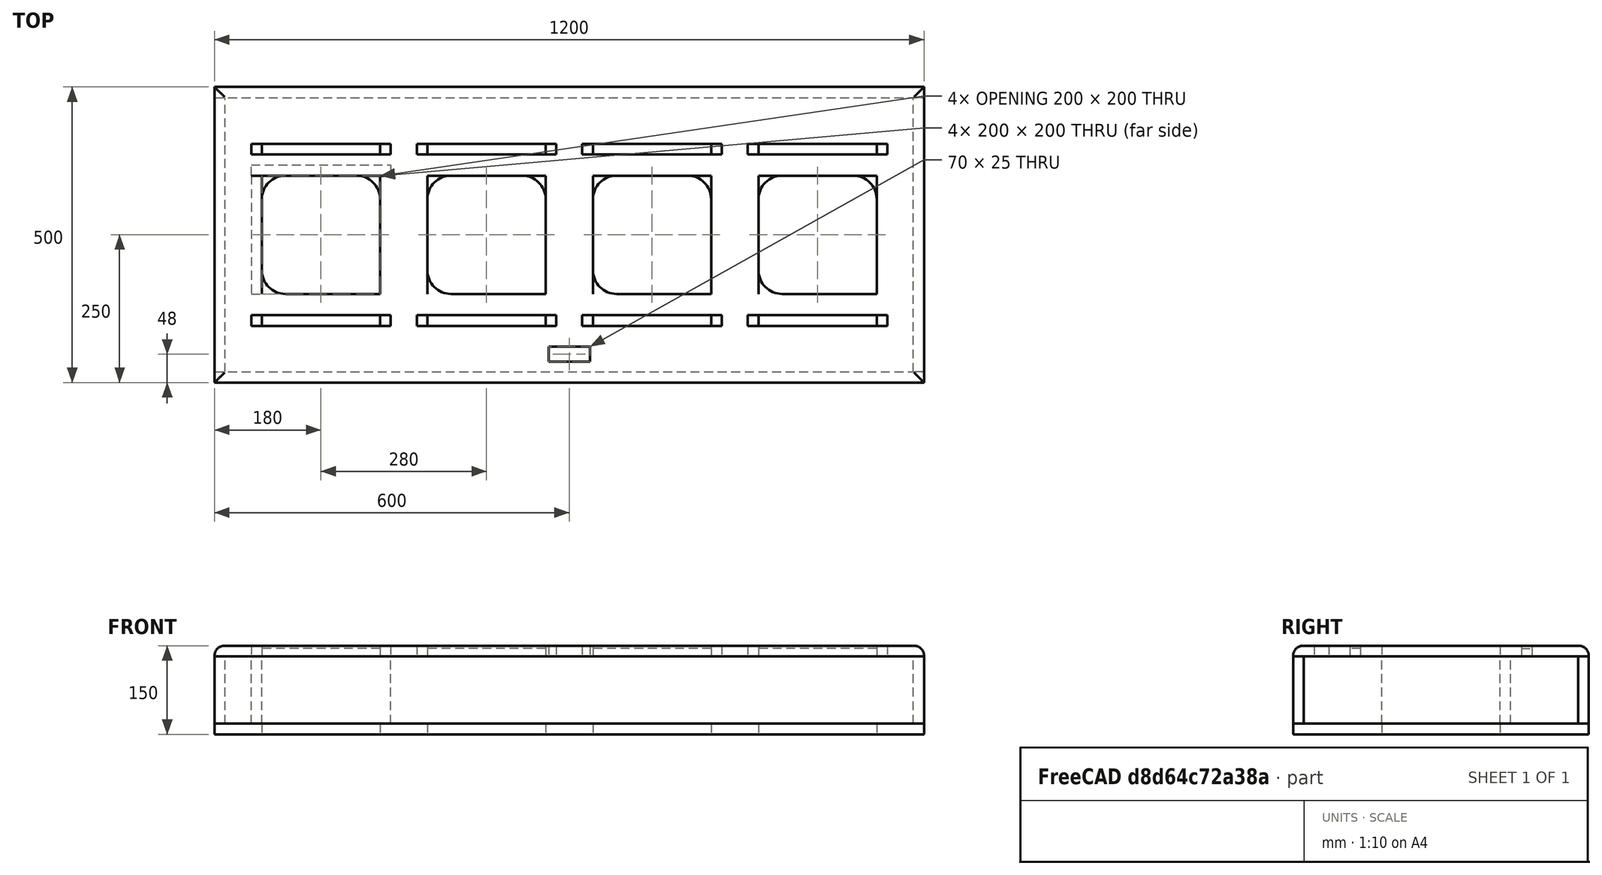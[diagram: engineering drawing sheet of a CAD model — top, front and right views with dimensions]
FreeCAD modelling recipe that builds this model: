
FCSTD DOCUMENT  (FreeCAD 0.18R16093 (Git))
Label: TonneV2
License: All rights reserved
LicenseURL: http://en.wikipedia.org/wiki/All_rights_reserved
objects: Sketcher::SketchObject×11, PartDesign::Body×8, TechDraw::DrawViewDimension×8, PartDesign::Pad×7, PartDesign::Pocket×4, PartDesign::LinearPattern×4, PartDesign::Mirrored×3, PartDesign::ShapeBinder×2, PartDesign::MultiTransform×2, PartDesign::Fillet×2, Spreadsheet::Sheet×1, PartDesign::FeatureBase×1, TechDraw::DrawSVGTemplate×1, TechDraw::DrawViewPart×1, TechDraw::DrawPage×1, App::DocumentObjectGroup×1
note: 55 computed .brp shape members not serialized (recipe doc carries the construction recipe); baked Part::Feature solids carry a one-line shape summary decoded from their .brp

FEATURE [Spreadsheet::Sheet] Spreadsheet  label="S"
  cells = A1=Höhe:; B1(Hoehe)=150; A2=Breite:; B2(Breite)=1200; A3=Tiefe:; B3(Tiefe)=500; A4=Materialdicke:; B4(Materialdicke)=18; A5=RandabstandLoch; B5(RandabstandLoch)=80; A6=Loch; B6(Loch)=200
FEATURE [Sketcher::SketchObject] Sketch
  MapMode = 5
  Support = -> [XY_Plane005]
  sketch-geometry (4):
    g0: LineSegment StartX=-600 StartY=250 StartZ=0 EndX=600 EndY=250 EndZ=0
    g1: LineSegment StartX=600 StartY=250 StartZ=0 EndX=600 EndY=-250 EndZ=0
    g2: LineSegment StartX=600 StartY=-250 StartZ=0 EndX=-600 EndY=-250 EndZ=0
    g3: LineSegment StartX=-600 StartY=-250 StartZ=0 EndX=-600 EndY=250 EndZ=0
  constraints (11):
    c: Coincident(g0,g1)
    c: Coincident(g1,g2)
    c: Coincident(g2,g3)
    c: Coincident(g3,g0)
    c: Horizontal(g0)
    c: Horizontal(g2)
    c: Vertical(g1)
    c: Vertical(g3)
    c: Symmetric(g1,g0,g-1)
    c: Distance(g0) = 1200
    c: Distance(g1) = 500
FEATURE [PartDesign::Pad] Pad
  Length = 18
  Length2 = 100
  Profile = -> Sketch
  Type = 0
FEATURE [Sketcher::SketchObject] Sketch006
  ExternalGeometry = -> [Pad]
  MapMode = 5
  Placement = pos=(0,0,18) rot=(0,0,1;0rad)
  Support = -> [Pad]
  sketch-geometry (4):
    g0: LineSegment StartX=-520 StartY=100 StartZ=0 EndX=-320 EndY=100 EndZ=0
    g1: LineSegment StartX=-320 StartY=100 StartZ=0 EndX=-320 EndY=-100 EndZ=0
    g2: LineSegment StartX=-320 StartY=-100 StartZ=0 EndX=-520 EndY=-100 EndZ=0
    g3: LineSegment StartX=-520 StartY=-100 StartZ=0 EndX=-520 EndY=100 EndZ=0
  constraints (12):
    c: Coincident(g0,g1)
    c: Coincident(g1,g2)
    c: Coincident(g2,g3)
    c: Coincident(g3,g0)
    c: Horizontal(g0)
    c: Horizontal(g2)
    c: Vertical(g1)
    c: Vertical(g3)
    c: Equal(g1,g2)
    c: Symmetric(g0,g1,g-1)
    c: Distance(g0) = 200
    c: DistanceX(g-3,g0) = 80
FEATURE [PartDesign::Pocket] Pocket
  BaseFeature = -> Pad
  Length = 5
  Length2 = 100
  Profile = -> Sketch006
  Type = 2
FEATURE [PartDesign::LinearPattern] LinearPattern
  BaseFeature = -> Pocket
  Direction = -> Sketch006 [H_Axis]
  Length = 840
  Occurrences = 4
  Originals = -> [Pocket]
FEATURE [PartDesign::Body] Body005  label="Boden"
  Group = -> [Sketch,Pad,Sketch006,Pocket,LinearPattern]
  Origin = -> Origin005
  Tip = -> LinearPattern
FEATURE [PartDesign::FeatureBase] BaseFeature
  BaseFeature = -> LinearPattern
FEATURE [Sketcher::SketchObject] Sketch007
  MapMode = 5
  Placement = pos=(0,0,0) rot=(1,0,0;1.5708rad)
  Support = -> [XZ_Plane006]
  sketch-geometry (4):
    g0: LineSegment StartX=-600 StartY=0 StartZ=0 EndX=600 EndY=0 EndZ=0
    g1: LineSegment StartX=600 StartY=0 StartZ=0 EndX=600 EndY=114 EndZ=0
    g2: LineSegment StartX=600 StartY=114 StartZ=0 EndX=-600 EndY=114 EndZ=0
    g3: LineSegment StartX=-600 StartY=114 StartZ=0 EndX=-600 EndY=0 EndZ=0
  constraints (11):
    c: Coincident(g0,g1)
    c: Coincident(g1,g2)
    c: Coincident(g2,g3)
    c: Coincident(g3,g0)
    c: Horizontal(g0)
    c: Horizontal(g2)
    c: Vertical(g1)
    c: Vertical(g3)
    c: Distance(g0) = 1200
    c: Distance(g3) = 114
    c: Symmetric(g0,g0,g-1)
FEATURE [PartDesign::Pad] Pad001
  Length = 18
  Length2 = 100
  Placement = pos=(0,0,0) rot=(1,0,0;1.5708rad)
  Profile = -> Sketch007
  Type = 0
FEATURE [PartDesign::Body] Body006  label="Backplate"
  Group = -> [Sketch007,Pad001]
  Origin = -> Origin006
  Placement = pos=(0,250,18) rot=(0,0,1;0rad)
  Tip = -> Pad001
FEATURE [Sketcher::SketchObject] Sketch008
  MapMode = 2
  Placement = pos=(0,0,0) rot=(1,0,0;1.5708rad)
  Support = -> [XZ_Plane007]
  sketch-geometry (4):
    g0: LineSegment StartX=-600 StartY=18 StartZ=0 EndX=600 EndY=18 EndZ=0
    g1: LineSegment StartX=600 StartY=18 StartZ=0 EndX=600 EndY=132 EndZ=0
    g2: LineSegment StartX=600 StartY=132 StartZ=0 EndX=-600 EndY=132 EndZ=0
    g3: LineSegment StartX=-600 StartY=132 StartZ=0 EndX=-600 EndY=18 EndZ=0
  constraints (12):
    c: Coincident(g0,g1)
    c: Coincident(g1,g2)
    c: Coincident(g2,g3)
    c: Coincident(g3,g0)
    c: Horizontal(g0)
    c: Horizontal(g2)
    c: Vertical(g1)
    c: Vertical(g3)
    c: Distance(g0) = 1200
    c: DistanceY(g-1,g0) = 18
    c: Distance(g3) = 114
    c: Symmetric(g0,g0,g-2)
FEATURE [PartDesign::Pad] Pad002
  Length = 18
  Length2 = 100
  Placement = pos=(0,0,0) rot=(1,0,0;1.5708rad)
  Profile = -> Sketch008
  Type = 0
FEATURE [PartDesign::Body] Body007  label="Faceplate"
  Group = -> [Sketch008,Pad002]
  Origin = -> Origin007
  Placement = pos=(0,-232,0) rot=(1,0,0;0rad)
  Tip = -> Pad002
FEATURE [Sketcher::SketchObject] Sketch009
  MapMode = 5
  Placement = pos=(0,0,0) rot=(0.57735,0.57735,0.57735;2.0944rad)
  Support = -> [YZ_Plane008]
  sketch-geometry (4):
    g0: LineSegment StartX=-232 StartY=0 StartZ=0 EndX=232 EndY=0 EndZ=0
    g1: LineSegment StartX=232 StartY=0 StartZ=0 EndX=232 EndY=114 EndZ=0
    g2: LineSegment StartX=232 StartY=114 StartZ=0 EndX=-232 EndY=114 EndZ=0
    g3: LineSegment StartX=-232 StartY=114 StartZ=0 EndX=-232 EndY=0 EndZ=0
  constraints (11):
    c: Coincident(g0,g1)
    c: Coincident(g1,g2)
    c: Coincident(g2,g3)
    c: Coincident(g3,g0)
    c: Horizontal(g0)
    c: Horizontal(g2)
    c: Vertical(g1)
    c: Vertical(g3)
    c: Distance(g0) = 464
    c: Distance(g1) = 114
    c: Symmetric(g0,g0,g-1)
FEATURE [PartDesign::Pad] Pad003
  Length = 18
  Length2 = 100
  Placement = pos=(0,0,0) rot=(0.57735,0.57735,0.57735;2.0944rad)
  Profile = -> Sketch009
  Reversed = true
  Type = 0
FEATURE [PartDesign::Body] Body008  label="Rechts"
  Group = -> [Sketch009,Pad003]
  Origin = -> Origin008
  Placement = pos=(600,0,18) rot=(0,0,1;0rad)
  Tip = -> Pad003
FEATURE [Sketcher::SketchObject] Sketch011
  MapMode = 5
  Placement = pos=(0,0,0) rot=(0.57735,0.57735,0.57735;2.0944rad)
  Support = -> [YZ_Plane009]
  sketch-geometry (4):
    g0: LineSegment StartX=-232 StartY=0 StartZ=0 EndX=232 EndY=0 EndZ=0
    g1: LineSegment StartX=232 StartY=0 StartZ=0 EndX=232 EndY=114 EndZ=0
    g2: LineSegment StartX=232 StartY=114 StartZ=0 EndX=-232 EndY=114 EndZ=0
    g3: LineSegment StartX=-232 StartY=114 StartZ=0 EndX=-232 EndY=0 EndZ=0
  constraints (11):
    c: Coincident(g0,g1)
    c: Coincident(g1,g2)
    c: Coincident(g2,g3)
    c: Coincident(g3,g0)
    c: Horizontal(g0)
    c: Horizontal(g2)
    c: Vertical(g1)
    c: Vertical(g3)
    c: Distance(g0) = 464
    c: Distance(g1) = 114
    c: Symmetric(g0,g0,g-1)
FEATURE [PartDesign::Pad] Pad004
  Length = 18
  Length2 = 100
  Placement = pos=(0,0,0) rot=(0.57735,0.57735,0.57735;2.0944rad)
  Profile = -> Sketch011
  Type = 0
FEATURE [PartDesign::Body] Body009  label="Links"
  Group = -> [Sketch011,Pad004]
  Origin = -> Origin009
  Placement = pos=(-600,0,18) rot=(0,0,1;0rad)
  Tip = -> Pad004
FEATURE [PartDesign::ShapeBinder] ShapeBinder
  Support = -> [LinearPattern]
  TraceSupport = false
FEATURE [Sketcher::SketchObject] Sketch012
  ExternalGeometry = -> [ShapeBinder]
  MapMode = 5
  Placement = pos=(0,0,18) rot=(0,0,1;0rad)
  Support = -> [ShapeBinder]
  sketch-geometry (4):
    g0: LineSegment StartX=-520 StartY=100 StartZ=0 EndX=-538 EndY=100 EndZ=0
    g1: LineSegment StartX=-538 StartY=100 StartZ=0 EndX=-538 EndY=-100 EndZ=0
    g2: LineSegment StartX=-538 StartY=-100 StartZ=0 EndX=-520 EndY=-100 EndZ=0
    g3: LineSegment StartX=-520 StartY=-100 StartZ=0 EndX=-520 EndY=100 EndZ=0
  constraints (11):
    c: Coincident(g0,g1)
    c: Coincident(g1,g2)
    c: Coincident(g3,g0)
    c: Horizontal(g0)
    c: Horizontal(g2)
    c: Vertical(g3)
    c: Coincident(g0,g-3)
    c: Distance(g0) = 18
    c: Coincident(g2,g3)
    c: Coincident(g-3,g2)
    c: Vertical(g1)
FEATURE [PartDesign::Pad] Pad005
  Length = 114
  Length2 = 100
  Profile = -> Sketch012
  Type = 0
FEATURE [PartDesign::Body] Body010  label="LochAbdeckungLinks"
  Group = -> [ShapeBinder,Sketch012,Pad005]
  Origin = -> Origin010
  Tip = -> Pad005
FEATURE [PartDesign::ShapeBinder] ShapeBinder001
  Support = -> [LinearPattern]
  TraceSupport = false
FEATURE [Sketcher::SketchObject] Sketch013
  ExternalGeometry = -> [ShapeBinder001]
  MapMode = 5
  Placement = pos=(0,0,18) rot=(0,0,1;0rad)
  Support = -> [ShapeBinder001]
  sketch-geometry (5):
    g0: LineSegment StartX=-538 StartY=118 StartZ=0 EndX=-302 EndY=118 EndZ=0
    g1: LineSegment StartX=-302 StartY=118 StartZ=0 EndX=-302 EndY=100 EndZ=0
    g2: LineSegment StartX=-302 StartY=100 StartZ=0 EndX=-538 EndY=100 EndZ=0
    g3: LineSegment StartX=-538 StartY=100 StartZ=0 EndX=-538 EndY=118 EndZ=0
    g4: LineSegment [constr] StartX=-420 StartY=125 StartZ=0 EndX=-420 EndY=75 EndZ=0
  constraints (15):
    c: Coincident(g0,g1)
    c: Coincident(g1,g2)
    c: Coincident(g2,g3)
    c: Coincident(g3,g0)
    c: Horizontal(g0)
    c: Horizontal(g2)
    c: Vertical(g1)
    c: Vertical(g3)
    c: PointOnObject(g-3,g2)
    c: Distance(g2,g-3) = 18
    c: Distance(g1) = 18
    c: Distance(g4) = 50
    c: Symmetric(g4,g4,g-3)
    c: Symmetric(g-3,g-3,g4)
    c: Symmetric(g1,g2,g4)
FEATURE [PartDesign::Pad] Pad006
  Length = 114
  Length2 = 100
  Profile = -> Sketch013
  Type = 0
FEATURE [PartDesign::Body] Body011  label="LochAbdeckungOben"
  Group = -> [ShapeBinder001,Sketch013,Pad006]
  Origin = -> Origin011
  Tip = -> Pad006
FEATURE [Sketcher::SketchObject] Sketch014
  ExternalGeometry = -> [BaseFeature]
  MapMode = 5
  Placement = pos=(0,0,18) rot=(0,0,1;0rad)
  Support = -> [BaseFeature]
  sketch-geometry (6):
    g0: LineSegment StartX=-538 StartY=154 StartZ=0 EndX=-302 EndY=154 EndZ=0
    g1: LineSegment StartX=-302 StartY=154 StartZ=0 EndX=-302 EndY=136 EndZ=0
    g2: LineSegment StartX=-302 StartY=136 StartZ=0 EndX=-538 EndY=136 EndZ=0
    g3: LineSegment StartX=-538 StartY=136 StartZ=0 EndX=-538 EndY=154 EndZ=0
    g4: LineSegment [constr] StartX=-538 StartY=136 StartZ=0 EndX=-520 EndY=100 EndZ=0
    g5: LineSegment [constr] StartX=-302 StartY=136 StartZ=0 EndX=-320 EndY=100 EndZ=0
  constraints (16):
    c: Coincident(g0,g1)
    c: Coincident(g1,g2)
    c: Coincident(g2,g3)
    c: Coincident(g3,g0)
    c: Horizontal(g0)
    c: Horizontal(g2)
    c: Vertical(g1)
    c: Vertical(g3)
    c: Distance(g2,g1) = 236
    c: DistanceY(g-3,g2) = 36
    c: Distance(g3) = 18
    c: Coincident(g4,g2)
    c: Coincident(g4,g-3)
    c: Coincident(g5,g1)
    c: Coincident(g5,g-3)
    c: Equal(g5,g4)
FEATURE [PartDesign::Pocket] Pocket001
  BaseFeature = -> BaseFeature
  Length = 5
  Length2 = 100
  Profile = -> Sketch014
  Type = 0
  expr: Length = 5
FEATURE [PartDesign::Mirrored] Mirrored
  MirrorPlane = -> XZ_Plane
FEATURE [PartDesign::LinearPattern] LinearPattern001
  Direction = -> Sketch014 [H_Axis]
  Length = 840
  Occurrences = 4
FEATURE [PartDesign::Mirrored] Mirrored001
  MirrorPlane = -> YZ_Plane
FEATURE [PartDesign::MultiTransform] MultiTransform
  BaseFeature = -> Pocket001
  Originals = -> [Pocket001]
  Transformations = -> [Mirrored,LinearPattern001,Mirrored001]
FEATURE [Sketcher::SketchObject] Sketch015
  ExternalGeometry = -> [MultiTransform]
  MapMode = 5
  Placement = pos=(0,-2.6903e-12,13) rot=(0,0,1;0rad)
  Support = -> [MultiTransform]
  sketch-geometry (4):
    g0: LineSegment StartX=-538 StartY=154 StartZ=0 EndX=-520 EndY=154 EndZ=0
    g1: LineSegment StartX=-520 StartY=154 StartZ=0 EndX=-520 EndY=136 EndZ=0
    g2: LineSegment StartX=-520 StartY=136 StartZ=0 EndX=-538 EndY=136 EndZ=0
    g3: LineSegment StartX=-538 StartY=136 StartZ=0 EndX=-538 EndY=154 EndZ=0
  constraints (11):
    c: Coincident(g0,g1)
    c: Coincident(g1,g2)
    c: Coincident(g2,g3)
    c: Coincident(g3,g0)
    c: Horizontal(g0)
    c: Horizontal(g2)
    c: Vertical(g1)
    c: Vertical(g3)
    c: Coincident(g0,g-4)
    c: Equal(g0,g1)
    c: Coincident(g2,g-4)
FEATURE [PartDesign::Pocket] Pocket002
  BaseFeature = -> MultiTransform
  Length = 5
  Length2 = 100
  Profile = -> Sketch015
  Type = 2
FEATURE [PartDesign::Mirrored] Mirrored002
  MirrorPlane = -> XZ_Plane
FEATURE [PartDesign::LinearPattern] LinearPattern003
  Direction = -> Sketch015 [H_Axis]
  Length = 840
  Occurrences = 4
FEATURE [PartDesign::LinearPattern] LinearPattern004
  Direction = -> Sketch015 [H_Axis]
  Length = 218
  Occurrences = 2
FEATURE [PartDesign::MultiTransform] MultiTransform001
  BaseFeature = -> Pocket002
  Originals = -> [Pocket002]
  Refine = true
  Transformations = -> [Mirrored002,LinearPattern003,LinearPattern004]
FEATURE [Sketcher::SketchObject] Sketch016
  ExternalGeometry = -> [MultiTransform001]
  MapMode = 5
  Placement = pos=(0,0,18) rot=(0,0,1;0rad)
  sketch-geometry (6):
    g0: LineSegment StartX=-35 StartY=-189.5 StartZ=0 EndX=35 EndY=-189.5 EndZ=0
    g1: LineSegment StartX=35 StartY=-189.5 StartZ=0 EndX=35 EndY=-214.5 EndZ=0
    g2: LineSegment StartX=35 StartY=-214.5 StartZ=0 EndX=-35 EndY=-214.5 EndZ=0
    g3: LineSegment StartX=-35 StartY=-214.5 StartZ=0 EndX=-35 EndY=-189.5 EndZ=0
    g4: LineSegment [constr] StartX=35 StartY=-189.5 StartZ=0 EndX=35 EndY=-154 EndZ=0
    g5: LineSegment [constr] StartX=35 StartY=-214.5 StartZ=0 EndX=35 EndY=-250 EndZ=0
  constraints (18):
    c: Coincident(g0,g1)
    c: Coincident(g1,g2)
    c: Coincident(g2,g3)
    c: Coincident(g3,g0)
    c: Horizontal(g0)
    c: Horizontal(g2)
    c: Vertical(g1)
    c: Vertical(g3)
    c: Symmetric(g1,g2,g-2)
    c: Distance(g3) = 25
    c: Coincident(g4,g0)
    c: PointOnObject(g4,g-4)
    c: Vertical(g4)
    c: Coincident(g5,g1)
    c: PointOnObject(g5,g-3)
    c: Vertical(g5)
    c: Equal(g4,g5)
    c: Distance(g0) = 70
FEATURE [PartDesign::Pocket] Pocket003
  BaseFeature = -> MultiTransform001
  Length = 5
  Length2 = 100
  Profile = -> Sketch016
  Type = 2
FEATURE [PartDesign::Fillet] Fillet
  Base = -> Pocket003 [Edge220,Edge219,Edge218,Edge185,Edge187,Edge188,Edge189,Edge191,Edge192,Edge233,Edge235,Edge236]
  BaseFeature = -> Pocket003
  Radius = 40
FEATURE [TechDraw::DrawSVGTemplate] Template  label="Page"
  EditableTexts = AUTHOR_NAME=Benjamin, Cindy, Marcel; DN=DN; DRAWING_TITLE=Obere Platte; FC-DATE=31/12/2018; FC-REV=REV A; FC-SC=Na; FC-SH=X / Y; FC-SI=A4; FreeCAD_DRAWING=Obere Platte mit Fillets; PN=PN
  Height = 210
  Orientation = 1
  Width = 297
FEATURE [PartDesign::Fillet] Fillet001
  Base = -> Fillet [Edge119,Edge122,Edge121,Edge117]
  BaseFeature = -> Fillet
  Radius = 17
  expr: Radius = Spreadsheet.Materialdicke - 1
FEATURE [PartDesign::Body] Body  label="Deckel"
  BaseFeature = -> LinearPattern
  Group = -> [BaseFeature,Sketch014,Pocket001,MultiTransform,Mirrored,LinearPattern001,Mirrored001,Sketch015,Pocket002,MultiTransform001,Mirrored002,Sketch016,LinearPattern003,LinearPattern004,Pocket003,Fillet,Fillet001]
  Origin = -> Origin
  Placement = pos=(0,0,132) rot=(0,0,1;0rad)
  Tip = -> Fillet001
FEATURE [TechDraw::DrawViewPart] View
  CoarseView = false
  Direction = (0,0,1)
  Focus = 100
  HardHidden = false
  IsoCount = 0
  IsoHidden = false
  IsoVisible = false
  LockPosition = false
  Perspective = false
  Rotation = 0
  Scale = 0.2
  ScaleType = 1
  SeamHidden = false
  SeamVisible = false
  SmoothHidden = false
  SmoothVisible = false
  Source = -> [Body]
  X = 151.663
  Y = 111.114
FEATURE [TechDraw::DrawViewDimension] Dimension
  Arbitrary = false
  FormatSpec = %.2f
  LockPosition = false
  MeasureType = 1
  OverTolerance = 0
  References2D = -> [View]
  Rotation = 0
  ScaleType = 0
  Type = 2
  UnderTolerance = 0
  X = -59.9147
  Y = 17.2189
FEATURE [TechDraw::DrawViewDimension] Dimension001
  Arbitrary = false
  FormatSpec = %.2f
  LockPosition = false
  MeasureType = 1
  OverTolerance = 0
  References2D = -> [View]
  Rotation = 0
  ScaleType = 0
  Type = 1
  UnderTolerance = 0
  X = -84.1616
  Y = 41.993
FEATURE [TechDraw::DrawViewDimension] Dimension002
  Arbitrary = false
  FormatSpec = %.2f
  LockPosition = false
  MeasureType = 1
  OverTolerance = 0
  References2D = -> [View]
  Rotation = 0
  ScaleType = 0
  Type = 2
  UnderTolerance = 0
  X = -79.4177
  Y = 4.91968
FEATURE [TechDraw::DrawViewDimension] Dimension003
  Arbitrary = false
  FormatSpec = %.2f
  LockPosition = false
  MeasureType = 1
  OverTolerance = 0
  References2D = -> [View]
  Rotation = 0
  ScaleType = 0
  Type = 1
  UnderTolerance = 0
  X = -82.756
  Y = -3.68976
FEATURE [TechDraw::DrawViewDimension] Dimension004
  Arbitrary = false
  FormatSpec = %.2f
  LockPosition = false
  MeasureType = 1
  OverTolerance = 0
  References2D = -> [View]
  Rotation = 0
  ScaleType = 0
  Type = 1
  UnderTolerance = 0
  X = -130.382
  Y = 2.63319
FEATURE [TechDraw::DrawViewDimension] Dimension005
  Arbitrary = false
  FormatSpec = %.2f
  LockPosition = false
  MeasureType = 1
  OverTolerance = 0
  References2D = -> [View]
  Rotation = 0
  ScaleType = 0
  Type = 1
  UnderTolerance = 0
  X = -54.2773
  Y = -18.2464
FEATURE [TechDraw::DrawViewDimension] Dimension006
  Arbitrary = false
  FormatSpec = %.2f
  LockPosition = false
  MeasureType = 1
  OverTolerance = 0
  References2D = -> [View]
  Rotation = 0
  ScaleType = 0
  Type = 1
  UnderTolerance = 0
  X = -0.225463
  Y = -44.4228
FEATURE [TechDraw::DrawViewDimension] Dimension007
  Arbitrary = false
  FormatSpec = %.2f
  LockPosition = false
  MeasureType = 1
  OverTolerance = 0
  References2D = -> [View]
  Rotation = 0
  ScaleType = 0
  Type = 2
  UnderTolerance = 0
  X = 30.8395
  Y = -39.7458
FEATURE [TechDraw::DrawPage] Page  label="TopPlate"
  KeepUpdated = true
  ProjectionType = 0
  Template = -> Template
  Views = -> [View,Dimension,Dimension001,Dimension002,Dimension003,Dimension004,Dimension005,Dimension006,Dimension007]
FEATURE [App::DocumentObjectGroup] Gruppe  label="TechDraws"
  Group = -> [Page]
